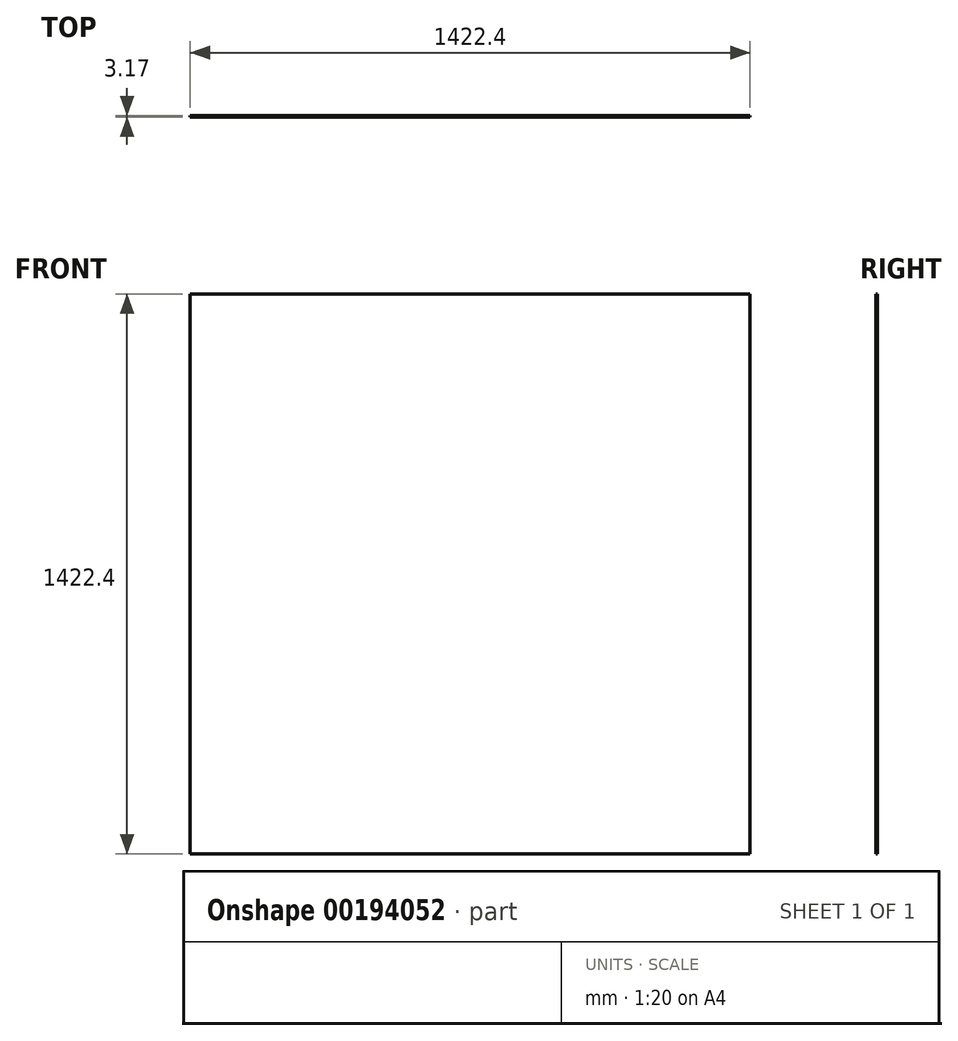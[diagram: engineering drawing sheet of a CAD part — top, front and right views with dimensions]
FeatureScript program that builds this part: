
annotation { "Feature Type Name" : "Feature", "Feature Type Description" : "" }
export const myFeature = defineFeature(function(context is Context, id is Id, definition is map)
    precondition{}
    {
        {
            var Q0;
            Q0=qCreatedBy(makeId("Front.planeOp"),FACE);
            var sketch = newSketch(context, id + "F0", { "sketchPlane" : qUnion([Q0])});
            skLineSegment(sketch, "E0.bottom", {"start": v(711.2, -711.2) * mm, "end": v(-711.2, -711.2) * mm});
            skLineSegment(sketch, "E0.top", {"start": v(711.2, 711.2) * mm, "end": v(-711.2, 711.2) * mm});
            skLineSegment(sketch, "E0.left", {"start": v(711.2, -711.2) * mm, "end": v(711.2, 711.2) * mm});
            skLineSegment(sketch, "E0.right", {"start": v(-711.2, -711.2) * mm, "end": v(-711.2, 711.2) * mm});
            skPoint(sketch, "E0.middle", {"position": v(0, 0) * mm});
            skSolve(sketch);
        }
        {
            var Q0;
            Q0=makeQuery(id+"F0.imprint","IMPRINT",FACE,{"disambiguationData":[TD([[makeQuery(id+"F0.imprint","IMPRINT",EDGE,{"derivedFrom":sQuery(id+"F0.wireOp",EDGE,"E0.bottom")}),-1.0]])]});
            extrude(context, id + "F1", {"entities" : qUnion([Q0]), "depth" : 3.17 * mm});
        }
    });
